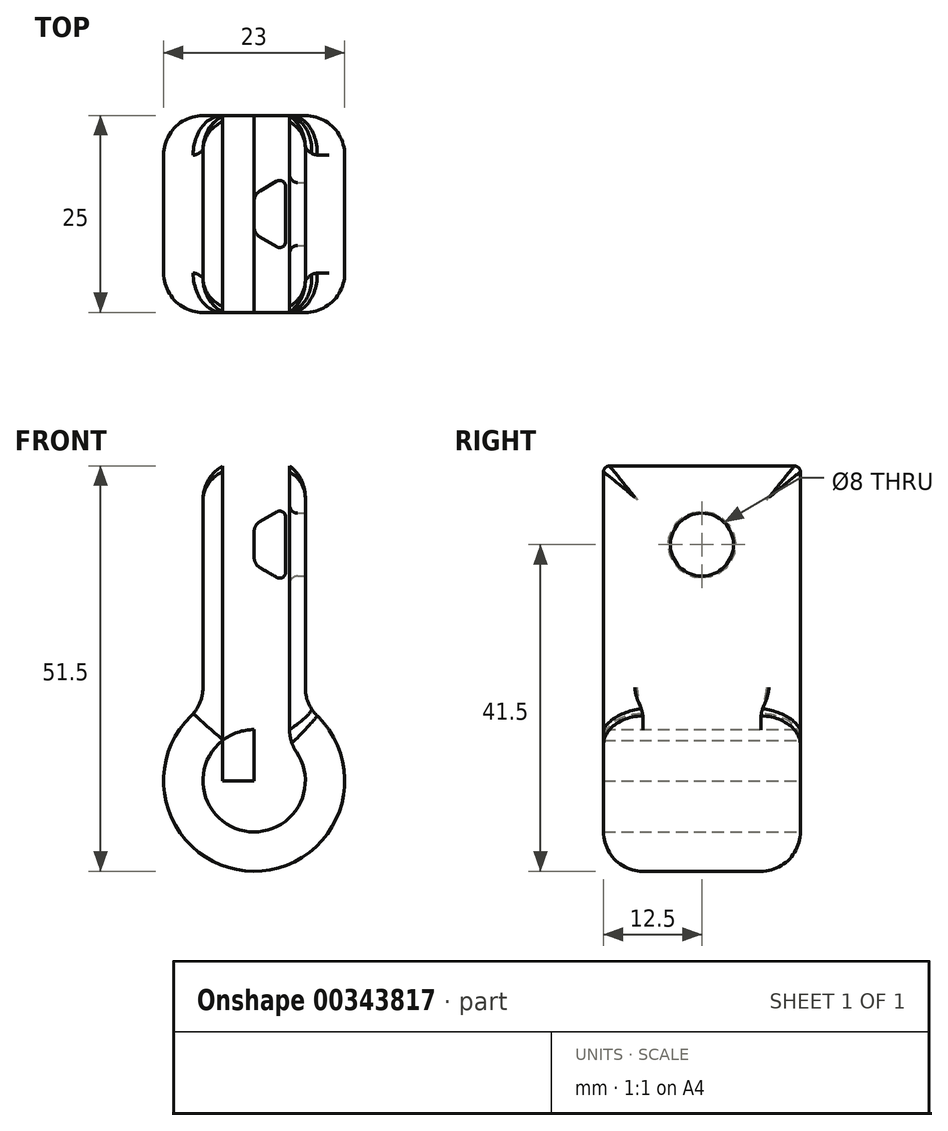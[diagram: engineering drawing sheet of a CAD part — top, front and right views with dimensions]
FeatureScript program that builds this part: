
annotation { "Feature Type Name" : "Feature", "Feature Type Description" : "" }
export const myFeature = defineFeature(function(context is Context, id is Id, definition is map)
    precondition{}
    {
        {
            var Q0;
            Q0=qCreatedBy(makeId("Front.planeOp"),FACE);
            var sketch = newSketch(context, id + "F0", { "sketchPlane" : qUnion([Q0])});
            skArc(sketch, "E0", {"start": v(-4, 5.12) * mm, "mid": v(0, -6.5) * mm, "end": v(4, 5.12) * mm});
            skArc(sketch, "E1.0", {"start": v(-4, 10.78) * mm, "mid": v(0, -11.5) * mm, "end": v(4, 10.78) * mm});
            skLineSegment(sketch, "E2.bottom", {"start": v(0, 0) * mm, "end": v(-6.5, 0) * mm});
            skLineSegment(sketch, "E2.top", {"start": v(0, 40) * mm, "end": v(-6.5, 40) * mm});
            skLineSegment(sketch, "E2.left", {"start": v(0, 0) * mm, "end": v(0, 40) * mm});
            skLineSegment(sketch, "E2.right", {"start": v(-6.5, 0) * mm, "end": v(-6.5, 40) * mm});
            skLineSegment(sketch, "E3.MirrorCS", {"start": v(6.5, 0) * mm, "end": v(6.5, 40) * mm});
            skLineSegment(sketch, "E4.MirrorCS", {"start": v(0, 40) * mm, "end": v(6.5, 40) * mm});
            skLineSegment(sketch, "E5.bottom", {"start": v(0, 0) * mm, "end": v(-2, 0) * mm});
            skLineSegment(sketch, "E5.top", {"start": v(0, 40) * mm, "end": v(-4, 40) * mm});
            skLineSegment(sketch, "E5.left", {"start": v(0, 0) * mm, "end": v(0, 6.5) * mm});
            skLineSegment(sketch, "E6.bottom", {"start": v(-4, 40) * mm, "end": v(0, 40) * mm});
            skLineSegment(sketch, "E6.top", {"start": v(-4, 0) * mm, "end": v(0, 0) * mm});
            skLineSegment(sketch, "E6.left", {"start": v(-4, 40) * mm, "end": v(-4, 0) * mm});
            skLineSegment(sketch, "E6.right", {"start": v(0, 40) * mm, "end": v(0, 0) * mm});
            skLineSegment(sketch, "E7.MirrorCS", {"start": v(4, 40) * mm, "end": v(4, 0) * mm});
            skArc(sketch, "E8", {"start": v(-4, 5.12) * mm, "mid": v(-2.12, 6.15) * mm, "end": v(0, 6.5) * mm});
            skLineSegment(sketch, "E9", {"start": v(4, 40) * mm, "end": v(4.5, 40) * mm});
            skLineSegment(sketch, "E10", {"start": v(4.5, 40) * mm, "end": v(4.5, 10.58) * mm});
            skLineSegment(sketch, "E11", {"start": v(4.5, 10.58) * mm, "end": v(4.5, 4.7) * mm});
            skSolve(sketch);
        }
        {
            var Q0;
            {var subQ0=sQuery(id+"F0.wireOp",EDGE,"E3.MirrorCS");var subQ5=sQuery(id+"F0.wireOp",EDGE,"E1.0");var subQ6=makeQuery(id+"F0.imprint","INTERSECT",VERTEX,{"derivedFrom":[subQ5,subQ0]});Q0=makeQuery(id+"F0.imprint","IMPRINT",FACE,{"disambiguationData":[TD([[makeQuery(id+"F0.imprint","IMPRINT",EDGE,{"disambiguationData":[TD([[subQ6,1.0]])],"derivedFrom":subQ5}),1.0]])]});}
            var Q1;
            {var subQ3=sQuery(id+"F0.wireOp",EDGE,"E2.right");var subQ5=sQuery(id+"F0.wireOp",EDGE,"E1.0");var subQ6=makeQuery(id+"F0.imprint","INTERSECT",VERTEX,{"derivedFrom":[subQ5,subQ3]});Q1=makeQuery(id+"F0.imprint","IMPRINT",FACE,{"disambiguationData":[TD([[makeQuery(id+"F0.imprint","IMPRINT",EDGE,{"disambiguationData":[TD([[subQ6,1.0]])],"derivedFrom":subQ5}),1.0]])]});}
            var Q2;
            {var subQ3=sQuery(id+"F0.wireOp",EDGE,"E11");Q2=makeQuery(id+"F0.imprint","IMPRINT",FACE,{"disambiguationData":[TD([[makeQuery(id+"F0.imprint","IMPRINT",EDGE,{"derivedFrom":subQ3}),1.0]])]});}
            var Q3;
            {var subQ0=sQuery(id+"F0.wireOp",EDGE,"E2.right");var subQ1=sQuery(id+"F0.wireOp",EDGE,"E1.0");var subQ2=makeQuery(id+"F0.imprint","INTERSECT",VERTEX,{"derivedFrom":[subQ1,subQ0]});Q3=makeQuery(id+"F0.imprint","IMPRINT",FACE,{"disambiguationData":[TD([[makeQuery(id+"F0.imprint","IMPRINT",EDGE,{"disambiguationData":[TD([[subQ2,1.0]])],"derivedFrom":subQ1}),-1.0]])]});}
            var Q4;
            {var subQ3=sQuery(id+"F0.wireOp",EDGE,"E10");Q4=makeQuery(id+"F0.imprint","IMPRINT",FACE,{"disambiguationData":[TD([[makeQuery(id+"F0.imprint","IMPRINT",EDGE,{"derivedFrom":subQ3}),1.0]])]});}
            var Q5;
            {var subQ6=sQuery(id+"F0.wireOp",EDGE,"E8");Q5=makeQuery(id+"F0.imprint","IMPRINT",FACE,{"disambiguationData":[TD([[makeQuery(id+"F0.imprint","IMPRINT",EDGE,{"derivedFrom":subQ6}),1.0]])]});}
            extrude(context, id + "F1", {"entities" : qUnion([Q0, Q1, Q2, Q3, Q4, Q5]), "depth" : 25 * mm, "offsetDistance" : 25 * mm});
        }
        {
            var Q0;
            Q0=makeQuery(id+"F1.opExtrude","SWEPT_FACE",FACE,{"disambiguationData":[OSD([sQuery(id+"F0.wireOp",EDGE,"E3.MirrorCS")])]});
            var sketch = newSketch(context, id + "F2", { "sketchPlane" : qUnion([Q0])});
            skLineSegment(sketch, "E12", {"start": v(-12.5, 40) * mm, "end": v(-12.5, 30) * mm});
            skCircle(sketch, "E13", {"center": v(-12.5, 30) * mm, "radius": 4 * mm});
            skSolve(sketch);
        }
        {
            var Q0;
            Q0=makeQuery(id+"F2.imprint","IMPRINT",FACE,{"disambiguationData":[TD([[makeQuery(id+"F2.imprint","IMPRINT",EDGE,{"derivedFrom":sQuery(id+"F2.wireOp",EDGE,"E13")}),1.0]])]});
            extrude(context, id + "F3", {"entities" : qUnion([Q0]), "operationType" : NewBodyOperationType.REMOVE, "oppositeDirection" : true, "depth" : 5 * mm, "offsetDistance" : 25 * mm});
        }
        {
            var Q0;
            Q0=makeQuery(id+"F1.opExtrude","SWEPT_FACE",FACE,{"disambiguationData":[OSD([sQuery(id+"F0.wireOp",EDGE,"E2.left")])]});
            var sketch = newSketch(context, id + "F4", { "sketchPlane" : qUnion([Q0])});
            skCircle(sketch, "E14.0", {"center": v(-12.5, 30) * mm, "radius": 4 * mm});
            skLineSegment(sketch, "E15.0", {"start": v(-5, 10.12) * mm, "end": v(-5, 35) * mm});
            skLineSegment(sketch, "E15.1", {"start": v(-20, 10.12) * mm, "end": v(-5, 10.12) * mm});
            skLineSegment(sketch, "E15.2", {"start": v(-20, 35) * mm, "end": v(-20, 10.12) * mm});
            skLineSegment(sketch, "E15.3", {"start": v(-5, 35) * mm, "end": v(-20, 35) * mm});
            skCircle(sketch, "E16", {"center": v(-12.5, 30) * mm, "radius": 2.5 * mm});
            skSolve(sketch);
        }
        {
            var Q0;
            Q0=makeQuery(id+"F4.imprint","IMPRINT",FACE,{"disambiguationData":[TD([[makeQuery(id+"F4.imprint","IMPRINT",EDGE,{"derivedFrom":sQuery(id+"F4.wireOp",EDGE,"E16")}),1.0]])]});
            extrude(context, id + "F5", {"entities" : qUnion([Q0]), "operationType" : NewBodyOperationType.ADD, "depth" : 4 * mm, "offsetDistance" : 25 * mm, "hasDraft" : true, "draftAngle" : 30 * degree});
        }
        {
            var Q0;
            Q0=makeQuery(id+"F5.opExtrude","CAP_EDGE",EDGE,{"disambiguationData":[OSD([sQuery(id+"F4.wireOp",EDGE,"E16")])],"isStart":false});
            var Q1;
            Q1=makeQuery(id+"F1.opExtrude","CAP_EDGE",EDGE,{"disambiguationData":[OSD([sQuery(id+"F0.wireOp",EDGE,"E2.top")])],"isStart":false});
            var Q2;
            Q2=makeQuery(id+"F1.opExtrude","CAP_EDGE",EDGE,{"disambiguationData":[OSD([sQuery(id+"F0.wireOp",EDGE,"E2.top")])],"isStart":true});
            var Q3;
            Q3=makeQuery(id+"F1.opExtrude","CAP_EDGE",EDGE,{"disambiguationData":[OSD([sQuery(id+"F0.wireOp",EDGE,"E4.MirrorCS")])],"isStart":true});
            var Q4;
            Q4=makeQuery(id+"F1.opExtrude","CAP_EDGE",EDGE,{"disambiguationData":[OSD([sQuery(id+"F0.wireOp",EDGE,"E4.MirrorCS")])],"isStart":false});
            fillet(context, id + "F6", {"entities" : qUnion([Q0, Q1, Q2, Q3, Q4]), "radius" : 0.75 * mm, "tangentPropagation" : true, "allowEdgeOverflow" : false});
        }
        {
            var Q0;
            Q0=makeQuery(id+"F1.opExtrude","SWEPT_EDGE",EDGE,{"disambiguationData":[OSD([sQuery(id+"F0.wireOp",EDGE,"E1.0"),sQuery(id+"F0.wireOp",EDGE,"E2.right")])]});
            var Q1;
            Q1=makeQuery(id+"F1.opExtrude","SWEPT_EDGE",EDGE,{"disambiguationData":[OSD([sQuery(id+"F0.wireOp",EDGE,"E1.0"),sQuery(id+"F0.wireOp",EDGE,"E3.MirrorCS")])]});
            var Q2;
            Q2=makeQuery(id+"F1.opExtrude","SWEPT_EDGE",EDGE,{"disambiguationData":[OSD([sQuery(id+"F0.wireOp",EDGE,"E0"),sQuery(id+"F0.wireOp",EDGE,"E11")])]});
            var Q3;
            Q3=makeQuery(id+"F1.opExtrude","SWEPT_EDGE",EDGE,{"disambiguationData":[OSD([sQuery(id+"F0.wireOp",EDGE,"E0"),sQuery(id+"F0.wireOp",EDGE,"E11")])]});
            fillet(context, id + "F7", {"entities" : qUnion([Q0, Q1, Q2, Q3]), "radius" : 5 * mm, "tangentPropagation" : true, "allowEdgeOverflow" : false});
        }
        {
            var Q0;
            Q0=makeQuery(id+"F5.opExtrude","CAP_EDGE",EDGE,{"disambiguationData":[OSD([sQuery(id+"F4.wireOp",EDGE,"E16")])],"isStart":true});
            fillet(context, id + "F8", {"entities" : qUnion([Q0]), "radius" : 1.5 * mm, "tangentPropagation" : true, "allowEdgeOverflow" : false});
        }
        {
            var Q0;
            Q0=makeQuery(id+"F3.boolean.opBoolean","INTERSECT",EDGE,{"derivedFrom":[makeQuery(id+"F1.opExtrude","SWEPT_FACE",FACE,{"disambiguationData":[OSD([sQuery(id+"F0.wireOp",EDGE,"E10"),sQuery(id+"F0.wireOp",EDGE,"E11")])]}),makeQuery(id+"F3.opExtrude","SWEPT_FACE",FACE,{"disambiguationData":[OSD([sQuery(id+"F2.wireOp",EDGE,"E13")])]})]});
            fillet(context, id + "F9", {"entities" : qUnion([Q0]), "radius" : 1 * mm, "tangentPropagation" : true, "allowEdgeOverflow" : false});
        }
        {
            var Q0;
            Q0=makeQuery(id+"F1.opExtrude","SWEPT_EDGE",EDGE,{"disambiguationData":[OSD([sQuery(id+"F0.wireOp",EDGE,"E2.left"),sQuery(id+"F0.wireOp",EDGE,"E8")])]});
            var Q1;
            Q1=makeQuery(id+"F1.opExtrude","SWEPT_EDGE",EDGE,{"disambiguationData":[OSD([sQuery(id+"F0.wireOp",EDGE,"E2.top"),sQuery(id+"F0.wireOp",EDGE,"E2.right")])]});
            fillet(context, id + "F10", {"entities" : qUnion([Q0, Q1]), "radius" : 5 * mm, "tangentPropagation" : true, "allowEdgeOverflow" : false});
        }
    });
